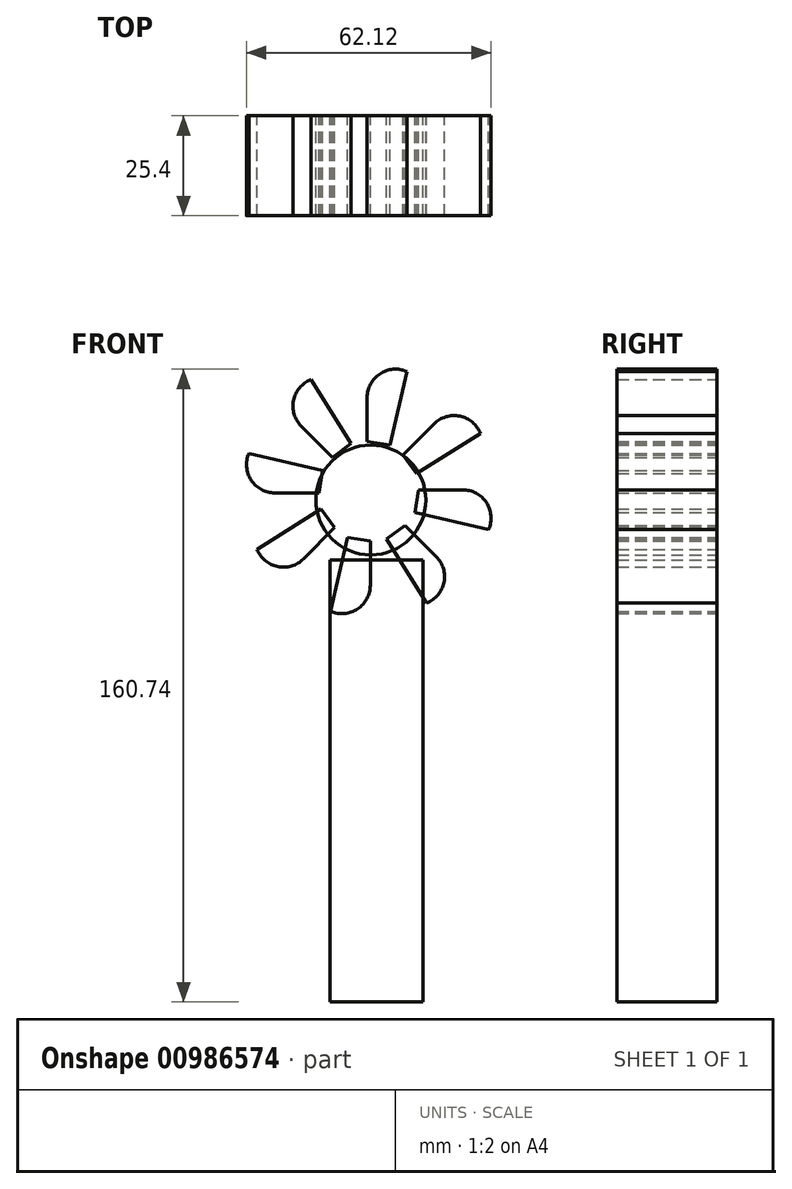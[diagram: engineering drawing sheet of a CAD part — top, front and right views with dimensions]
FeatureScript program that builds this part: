
annotation { "Feature Type Name" : "Feature", "Feature Type Description" : "" }
export const myFeature = defineFeature(function(context is Context, id is Id, definition is map)
    precondition{}
    {
        {
            var Q0;
            Q0=qCreatedBy(makeId("Front.planeOp"),FACE);
            var sketch = newSketch(context, id + "F0", { "sketchPlane" : qUnion([Q0])});
            skLineSegment(sketch, "E0.bottom", {"start": v(-4.75, 40.72) * mm, "end": v(18.85, 40.72) * mm});
            skLineSegment(sketch, "E0.top", {"start": v(-4.75, -71.52) * mm, "end": v(18.85, -71.52) * mm});
            skLineSegment(sketch, "E0.left", {"start": v(-4.75, 40.72) * mm, "end": v(-4.75, -71.52) * mm});
            skLineSegment(sketch, "E0.right", {"start": v(18.85, 40.72) * mm, "end": v(18.85, -71.52) * mm});
            skSolve(sketch);
        }
        {
            var Q0;
            Q0 = qSketchRegion(id + "F0", true);
            extrude(context, id + "F1", {"entities" : qUnion([Q0]), "depth" : 25.4 * mm, "offsetDistance" : 25.4 * mm});
        }
        {
            var Q0;
            Q0=qCreatedBy(makeId("Front.planeOp"),FACE);
            var sketch = newSketch(context, id + "F2", { "sketchPlane" : qUnion([Q0])});
            skCircle(sketch, "E1", {"center": v(5.61, 55.98) * mm, "radius": 13.97 * mm});
            skSolve(sketch);
        }
        {
            var Q0;
            Q0 = qSketchRegion(id + "F2", true);
            extrude(context, id + "F3", {"entities" : qUnion([Q0]), "depth" : 25.4 * mm, "offsetDistance" : 25.4 * mm});
        }
        {
            var Q0;
            Q0=qCreatedBy(makeId("Front.planeOp"),FACE);
            var sketch = newSketch(context, id + "F4", { "sketchPlane" : qUnion([Q0])});
            skLineSegment(sketch, "E2", {"start": v(16.84, 52.81) * mm, "end": v(35.54, 48.5) * mm});
            skLineSegment(sketch, "E3", {"start": v(28.92, 58.57) * mm, "end": v(17.7, 58.57) * mm});
            skArc(sketch, "E4", {"start": v(35.54, 48.5) * mm, "mid": v(34.95, 55.32) * mm, "end": v(28.92, 58.57) * mm});
            skLineSegment(sketch, "E5", {"start": v(17.7, 58.57) * mm, "end": v(16.84, 52.81) * mm});
            skLineSegment(sketch, "E6.1.0", {"start": v(17.18, 62.7) * mm, "end": v(33.46, 72.87) * mm});
            skLineSegment(sketch, "E6.1.1", {"start": v(21.66, 75.31) * mm, "end": v(13.72, 67.37) * mm});
            skArc(sketch, "E6.1.2", {"start": v(33.46, 72.87) * mm, "mid": v(28.22, 77.27) * mm, "end": v(21.66, 75.31) * mm});
            skLineSegment(sketch, "E6.1.3", {"start": v(13.72, 67.37) * mm, "end": v(17.18, 62.7) * mm});
            skLineSegment(sketch, "E6.2.0", {"start": v(10.43, 69.92) * mm, "end": v(14.75, 88.63) * mm});
            skLineSegment(sketch, "E6.2.1", {"start": v(4.68, 82.01) * mm, "end": v(4.68, 70.79) * mm});
            skArc(sketch, "E6.2.2", {"start": v(14.75, 88.63) * mm, "mid": v(7.93, 88.04) * mm, "end": v(4.68, 82.01) * mm});
            skLineSegment(sketch, "E6.2.3", {"start": v(4.68, 70.79) * mm, "end": v(10.43, 69.92) * mm});
            skPoint(sketch, "E6.center", {"position": v(5.08, 58.17) * mm});
            skLineSegment(sketch, "E7.1.3.0", {"start": v(0.55, 70.26) * mm, "end": v(-9.62, 86.55) * mm});
            skLineSegment(sketch, "E7.3.3.0", {"start": v(-12.07, 74.74) * mm, "end": v(-4.13, 66.8) * mm});
            skArc(sketch, "E7.6.3.0", {"start": v(-9.62, 86.55) * mm, "mid": v(-14.03, 81.3) * mm, "end": v(-12.07, 74.74) * mm});
            skLineSegment(sketch, "E7.10.3.0", {"start": v(-4.13, 66.8) * mm, "end": v(0.55, 70.26) * mm});
            skLineSegment(sketch, "E7.1.4.0", {"start": v(-6.68, 63.52) * mm, "end": v(-25.38, 67.84) * mm});
            skLineSegment(sketch, "E7.3.4.0", {"start": v(-18.76, 57.76) * mm, "end": v(-7.54, 57.76) * mm});
            skArc(sketch, "E7.6.4.0", {"start": v(-25.38, 67.84) * mm, "mid": v(-24.8, 61.01) * mm, "end": v(-18.76, 57.76) * mm});
            skLineSegment(sketch, "E7.10.4.0", {"start": v(-7.54, 57.76) * mm, "end": v(-6.68, 63.52) * mm});
            skLineSegment(sketch, "E7.1.5.0", {"start": v(-7.02, 53.64) * mm, "end": v(-23.3, 43.46) * mm});
            skLineSegment(sketch, "E7.3.5.0", {"start": v(-11.5, 41.02) * mm, "end": v(-3.56, 48.96) * mm});
            skArc(sketch, "E7.6.5.0", {"start": v(-23.3, 43.46) * mm, "mid": v(-18.06, 39.06) * mm, "end": v(-11.5, 41.02) * mm});
            skLineSegment(sketch, "E7.10.5.0", {"start": v(-3.56, 48.96) * mm, "end": v(-7.02, 53.64) * mm});
            skLineSegment(sketch, "E7.1.6.0", {"start": v(-0.27, 46.4) * mm, "end": v(-4.6, 27.7) * mm});
            skLineSegment(sketch, "E7.3.6.0", {"start": v(5.48, 34.32) * mm, "end": v(5.48, 45.55) * mm});
            skArc(sketch, "E7.6.6.0", {"start": v(-4.6, 27.7) * mm, "mid": v(2.23, 28.3) * mm, "end": v(5.48, 34.32) * mm});
            skLineSegment(sketch, "E7.10.6.0", {"start": v(5.48, 45.55) * mm, "end": v(-0.27, 46.4) * mm});
            skLineSegment(sketch, "E7.1.7.0", {"start": v(9.6, 46.07) * mm, "end": v(19.78, 29.79) * mm});
            skLineSegment(sketch, "E7.3.7.0", {"start": v(22.23, 41.6) * mm, "end": v(14.29, 49.53) * mm});
            skArc(sketch, "E7.6.7.0", {"start": v(19.78, 29.79) * mm, "mid": v(24.19, 35.03) * mm, "end": v(22.23, 41.6) * mm});
            skLineSegment(sketch, "E7.10.7.0", {"start": v(14.29, 49.53) * mm, "end": v(9.6, 46.07) * mm});
            skSolve(sketch);
        }
        {
            var Q0;
            Q0=makeQuery(id+"F4.imprint","IMPRINT",FACE,{"disambiguationData":[TD([[makeQuery(id+"F4.imprint","IMPRINT",EDGE,{"derivedFrom":sQuery(id+"F4.wireOp",EDGE,"E7.1.5.0")}),1.0]])]});
            var Q1;
            Q1=makeQuery(id+"F4.imprint","IMPRINT",FACE,{"disambiguationData":[TD([[makeQuery(id+"F4.imprint","IMPRINT",EDGE,{"derivedFrom":sQuery(id+"F4.wireOp",EDGE,"E7.1.4.0")}),1.0]])]});
            var Q2;
            Q2=makeQuery(id+"F4.imprint","IMPRINT",FACE,{"disambiguationData":[TD([[makeQuery(id+"F4.imprint","IMPRINT",EDGE,{"derivedFrom":sQuery(id+"F4.wireOp",EDGE,"E7.1.3.0")}),1.0]])]});
            var Q3;
            Q3=makeQuery(id+"F4.imprint","IMPRINT",FACE,{"disambiguationData":[TD([[makeQuery(id+"F4.imprint","IMPRINT",EDGE,{"derivedFrom":sQuery(id+"F4.wireOp",EDGE,"E6.2.0")}),1.0]])]});
            var Q4;
            Q4=makeQuery(id+"F4.imprint","IMPRINT",FACE,{"disambiguationData":[TD([[makeQuery(id+"F4.imprint","IMPRINT",EDGE,{"derivedFrom":sQuery(id+"F4.wireOp",EDGE,"E6.1.0")}),1.0]])]});
            var Q5;
            Q5=makeQuery(id+"F4.imprint","IMPRINT",FACE,{"disambiguationData":[TD([[makeQuery(id+"F4.imprint","IMPRINT",EDGE,{"derivedFrom":sQuery(id+"F4.wireOp",EDGE,"E2")}),1.0]])]});
            var Q6;
            Q6=makeQuery(id+"F4.imprint","IMPRINT",FACE,{"disambiguationData":[TD([[makeQuery(id+"F4.imprint","IMPRINT",EDGE,{"derivedFrom":sQuery(id+"F4.wireOp",EDGE,"E7.1.7.0")}),1.0]])]});
            var Q7;
            Q7=makeQuery(id+"F4.imprint","IMPRINT",FACE,{"disambiguationData":[TD([[makeQuery(id+"F4.imprint","IMPRINT",EDGE,{"derivedFrom":sQuery(id+"F4.wireOp",EDGE,"E7.1.6.0")}),1.0]])]});
            extrude(context, id + "F5", {"entities" : qUnion([Q0, Q1, Q2, Q3, Q4, Q5, Q6, Q7]), "depth" : 25.4 * mm, "offsetDistance" : 25.4 * mm});
        }
    });
